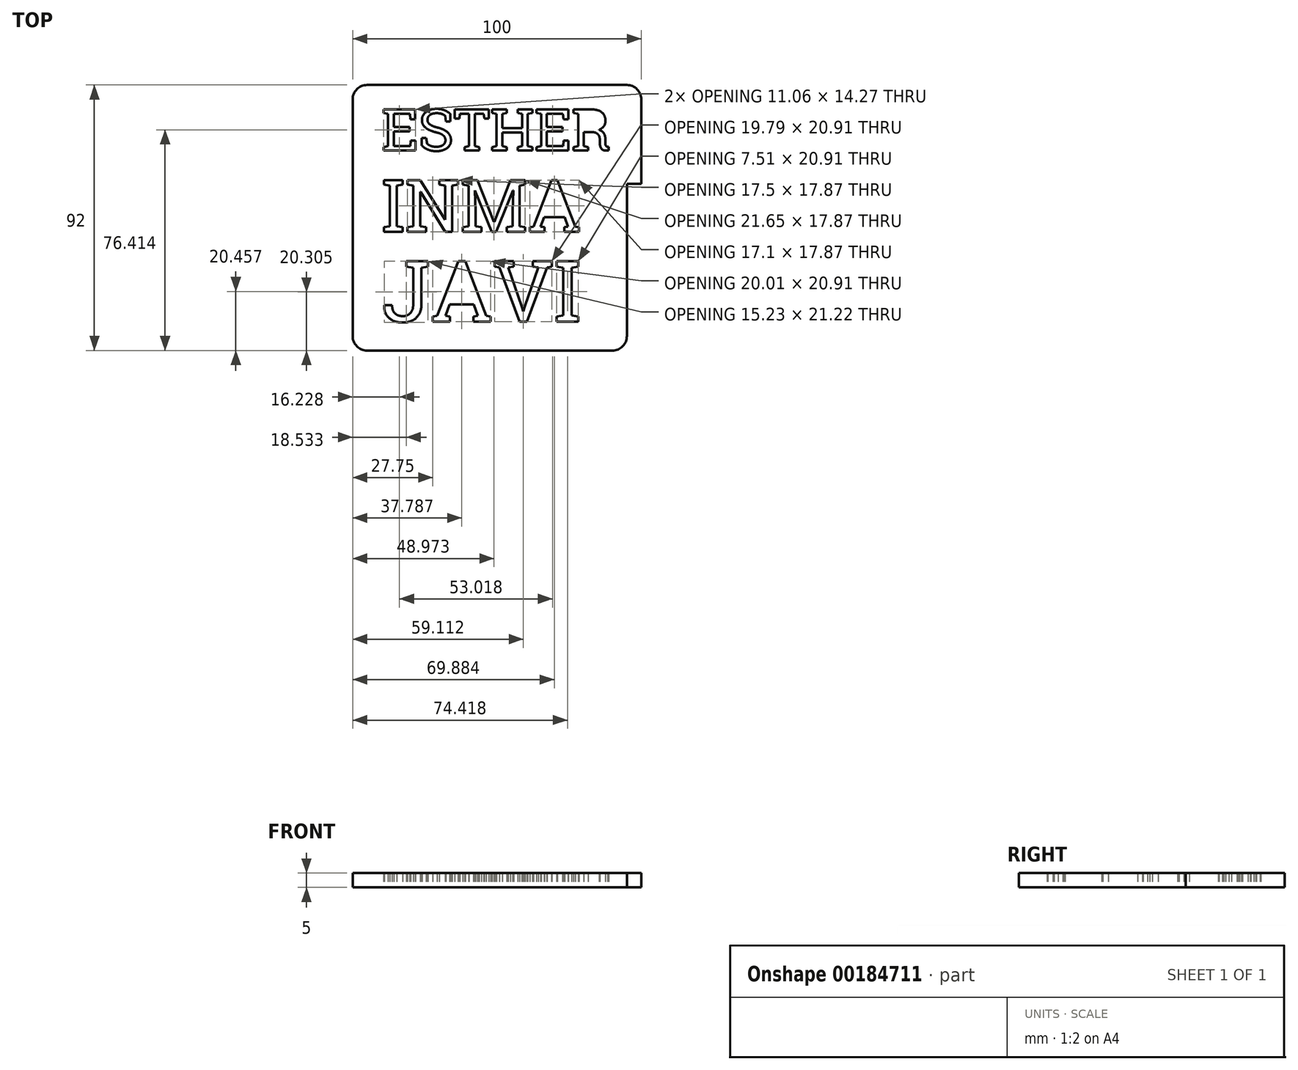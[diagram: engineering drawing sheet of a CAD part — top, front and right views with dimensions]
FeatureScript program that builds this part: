
annotation { "Feature Type Name" : "Feature", "Feature Type Description" : "" }
export const myFeature = defineFeature(function(context is Context, id is Id, definition is map)
    precondition{}
    {
        {
            var Q0;
            Q0=qCreatedBy(makeId("Top.planeOp"),FACE);
            var sketch = newSketch(context, id + "F0", { "sketchPlane" : qUnion([Q0])});
            skLineSegment(sketch, "E0.bottom", {"start": v(5, 0) * mm, "end": v(90, 0) * mm});
            skLineSegment(sketch, "E0.top", {"start": v(5, 92) * mm, "end": v(95, 92) * mm});
            skLineSegment(sketch, "E0.left", {"start": v(0, 5) * mm, "end": v(0, 87) * mm});
            skLineSegment(sketch, "E0.right", {"start": v(100, 0) * mm, "end": v(100, 87) * mm});
            skText(sketch, "E1", { "text": "JAVI", "fontName": "RobotoSlab-Regular.ttf"});
            skText(sketch, "E2", { "text": "INMA", "fontName": "RobotoSlab-Regular.ttf"});
            skText(sketch, "E3", { "text": "ESTHER", "fontName": "RobotoSlab-Regular.ttf"});
            skLineSegment(sketch, "E4.bottom", {"start": v(100, 0) * mm, "end": v(95, 0) * mm});
            skLineSegment(sketch, "E4.top", {"start": v(100, 57.78) * mm, "end": v(95, 57.78) * mm});
            skLineSegment(sketch, "E4.left", {"start": v(100, 0) * mm, "end": v(100, 57.78) * mm});
            skLineSegment(sketch, "E4.right", {"start": v(95, 5) * mm, "end": v(95, 57.78) * mm});
            skPoint(sketch, "E5.visualSharp", {"position": v(100, 92) * mm});
            skArc(sketch, "E5.filletArc", {"start": v(100, 87) * mm, "mid": v(98.54, 90.54) * mm, "end": v(95, 92) * mm});
            skPoint(sketch, "E6.visualSharp", {"position": v(0, 92) * mm});
            skArc(sketch, "E6.filletArc", {"start": v(5, 92) * mm, "mid": v(1.46, 90.54) * mm, "end": v(0, 87) * mm});
            skPoint(sketch, "E7.visualSharp", {"position": v(0, 0) * mm});
            skArc(sketch, "E7.filletArc", {"start": v(0, 5) * mm, "mid": v(1.46, 1.46) * mm, "end": v(5, 0) * mm});
            skArc(sketch, "E8.filletArc", {"start": v(90, 0) * mm, "mid": v(93.54, 1.46) * mm, "end": v(95, 5) * mm});
            const initialGuessF0  = {"E1": [0.01, 0.01, 1, 0, 0.02118], "E2": [0.01, 0.04118, 1, 0, 0.0181], "E3": [0.01, 0.06928, 1, 0, 0.01445]};
            skSetInitialGuess(sketch, initialGuessF0);
            skSolve(sketch);
        }
        {
            var Q0;
            Q0=makeQuery(id+"F0.imprint","IMPRINT",FACE,{"disambiguationData":[TD([[makeQuery(id+"F0.imprint","IMPRINT",EDGE,{"derivedFrom":sQuery(id+"F0.wireOp",EDGE,"E0.bottom")}),1.0]])]});
            extrude(context, id + "F1", {"entities" : qUnion([Q0]), "depth" : 5 * mm});
        }
        {
            var Q0;
            Q0=makeQuery(id+"F0.imprint","IMPRINT",FACE,{"disambiguationData":[TD([[makeQuery(id+"F0.imprint","IMPRINT",EDGE,{"derivedFrom":sQuery(id+"F0.wireOp",EDGE,"E3.sketch_text.stroke-0")}),-1.0]])]});
            var Q1;
            Q1=makeQuery(id+"F0.imprint","IMPRINT",FACE,{"disambiguationData":[TD([[makeQuery(id+"F0.imprint","IMPRINT",EDGE,{"derivedFrom":sQuery(id+"F0.wireOp",EDGE,"E3.sketch_text.stroke-20")}),-1.0]])]});
            var Q2;
            Q2=makeQuery(id+"F0.imprint","IMPRINT",FACE,{"disambiguationData":[TD([[makeQuery(id+"F0.imprint","IMPRINT",EDGE,{"derivedFrom":sQuery(id+"F0.wireOp",EDGE,"E3.sketch_text.stroke-50")}),-1.0]])]});
            var Q3;
            Q3=makeQuery(id+"F0.imprint","IMPRINT",FACE,{"disambiguationData":[TD([[makeQuery(id+"F0.imprint","IMPRINT",EDGE,{"derivedFrom":sQuery(id+"F0.wireOp",EDGE,"E3.sketch_text.stroke-66")}),-1.0]])]});
            var Q4;
            Q4=makeQuery(id+"F0.imprint","IMPRINT",FACE,{"disambiguationData":[TD([[makeQuery(id+"F0.imprint","IMPRINT",EDGE,{"derivedFrom":sQuery(id+"F0.wireOp",EDGE,"E3.sketch_text.stroke-96")}),-1.0]])]});
            var Q5;
            Q5=makeQuery(id+"F0.imprint","IMPRINT",FACE,{"disambiguationData":[TD([[makeQuery(id+"F0.imprint","IMPRINT",EDGE,{"derivedFrom":sQuery(id+"F0.wireOp",EDGE,"E3.sketch_text.stroke-116")}),-1.0]])]});
            var Q6;
            Q6=makeQuery(id+"F0.imprint","IMPRINT",FACE,{"disambiguationData":[TD([[makeQuery(id+"F0.imprint","IMPRINT",EDGE,{"derivedFrom":sQuery(id+"F0.wireOp",EDGE,"E2.sketch_text.stroke-0")}),-1.0]])]});
            var Q7;
            Q7=makeQuery(id+"F0.imprint","IMPRINT",FACE,{"disambiguationData":[TD([[makeQuery(id+"F0.imprint","IMPRINT",EDGE,{"derivedFrom":sQuery(id+"F0.wireOp",EDGE,"E2.sketch_text.stroke-12")}),-1.0]])]});
            var Q8;
            Q8=makeQuery(id+"F0.imprint","IMPRINT",FACE,{"disambiguationData":[TD([[makeQuery(id+"F0.imprint","IMPRINT",EDGE,{"derivedFrom":sQuery(id+"F0.wireOp",EDGE,"E2.sketch_text.stroke-36")}),-1.0]])]});
            var Q9;
            Q9=makeQuery(id+"F0.imprint","IMPRINT",FACE,{"disambiguationData":[TD([[makeQuery(id+"F0.imprint","IMPRINT",EDGE,{"derivedFrom":sQuery(id+"F0.wireOp",EDGE,"E2.sketch_text.stroke-67")}),-1.0]])]});
            var Q10;
            Q10=makeQuery(id+"F0.imprint","IMPRINT",FACE,{"disambiguationData":[TD([[makeQuery(id+"F0.imprint","IMPRINT",EDGE,{"derivedFrom":sQuery(id+"F0.wireOp",EDGE,"E1.sketch_text.stroke-0")}),-1.0]])]});
            var Q11;
            Q11=makeQuery(id+"F0.imprint","IMPRINT",FACE,{"disambiguationData":[TD([[makeQuery(id+"F0.imprint","IMPRINT",EDGE,{"derivedFrom":sQuery(id+"F0.wireOp",EDGE,"E1.sketch_text.stroke-18")}),-1.0]])]});
            var Q12;
            Q12=makeQuery(id+"F0.imprint","IMPRINT",FACE,{"disambiguationData":[TD([[makeQuery(id+"F0.imprint","IMPRINT",EDGE,{"derivedFrom":sQuery(id+"F0.wireOp",EDGE,"E1.sketch_text.stroke-38")}),-1.0]])]});
            var Q13;
            Q13=makeQuery(id+"F0.imprint","IMPRINT",FACE,{"disambiguationData":[TD([[makeQuery(id+"F0.imprint","IMPRINT",EDGE,{"derivedFrom":sQuery(id+"F0.wireOp",EDGE,"E1.sketch_text.stroke-56")}),-1.0]])]});
            extrude(context, id + "F2", {"entities" : qUnion([Q0, Q1, Q2, Q3, Q4, Q5, Q6, Q7, Q8, Q9, Q10, Q11, Q12, Q13]), "operationType" : NewBodyOperationType.REMOVE, "depth" : 5 * mm});
        }
    });
